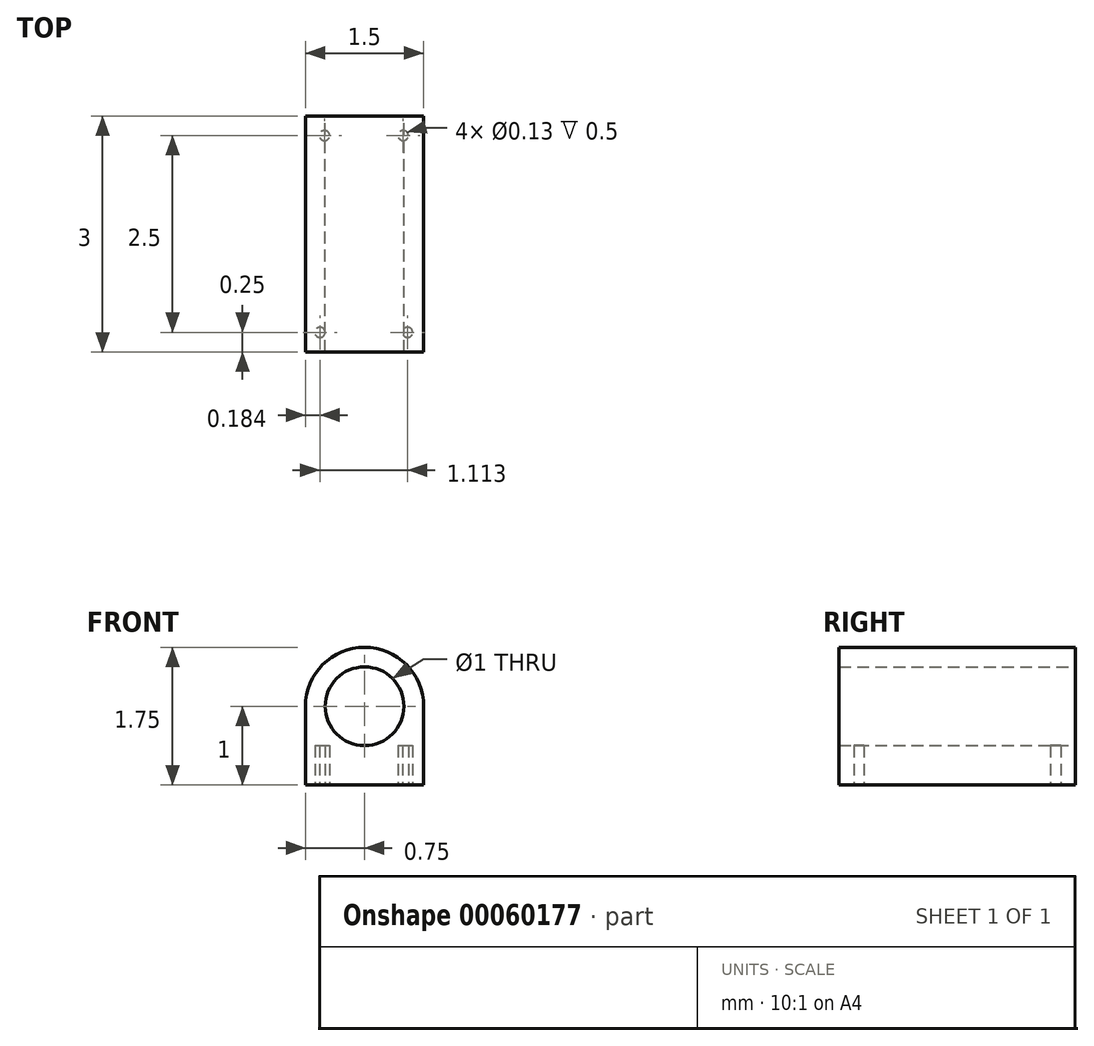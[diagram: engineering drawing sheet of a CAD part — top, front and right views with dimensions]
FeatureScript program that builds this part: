
annotation { "Feature Type Name" : "Feature", "Feature Type Description" : "" }
export const myFeature = defineFeature(function(context is Context, id is Id, definition is map)
    precondition{}
    {
        {
            var Q0;
            Q0=qCreatedBy(makeId("Front.planeOp"),FACE);
            var sketch = newSketch(context, id + "F0", { "sketchPlane" : qUnion([Q0])});
            skLineSegment(sketch, "E0.top", {"start": v(-0.75, -1) * mm, "end": v(0.75, -1) * mm});
            skLineSegment(sketch, "E0.left", {"start": v(-0.75, 0) * mm, "end": v(-0.75, -1) * mm});
            skLineSegment(sketch, "E0.right", {"start": v(0.75, 0) * mm, "end": v(0.75, -1) * mm});
            skArc(sketch, "E1", {"start": v(0.75, 0) * mm, "mid": v(0, 0.75) * mm, "end": v(-0.75, 0) * mm});
            skCircle(sketch, "E2", {"center": v(0, 0) * mm, "radius": 0.5 * mm});
            skSolve(sketch);
        }
        {
            var Q0;
            Q0 = qSketchRegion(id + "F0", true);
            extrude(context, id + "F1", {"entities" : qUnion([Q0]), "endBound" : BoundingType.SYMMETRIC, "depth" : 3 * mm});
        }
        {
            var Q0;
            Q0=makeQuery(id+"F1.opExtrude","SWEPT_FACE",FACE,{"disambiguationData":[OSD([sQuery(id+"F0.wireOp",EDGE,"E0.top")])]});
            var sketch = newSketch(context, id + "F2", { "sketchPlane" : qUnion([Q0])});
            skCircle(sketch, "E3", {"center": v(-0.57, 1.25) * mm, "radius": 0.07 * mm});
            skCircle(sketch, "E4", {"center": v(0.55, 1.25) * mm, "radius": 0.07 * mm});
            skCircle(sketch, "E5", {"center": v(-0.5, -1.25) * mm, "radius": 0.07 * mm});
            skCircle(sketch, "E6", {"center": v(0.5, -1.25) * mm, "radius": 0.07 * mm});
            skSolve(sketch);
        }
        {
            var Q0;
            Q0 = qSketchRegion(id + "F2", true);
            extrude(context, id + "F3", {"entities" : qUnion([Q0]), "operationType" : NewBodyOperationType.REMOVE, "oppositeDirection" : true, "depth" : 0.5 * mm});
        }
    });
